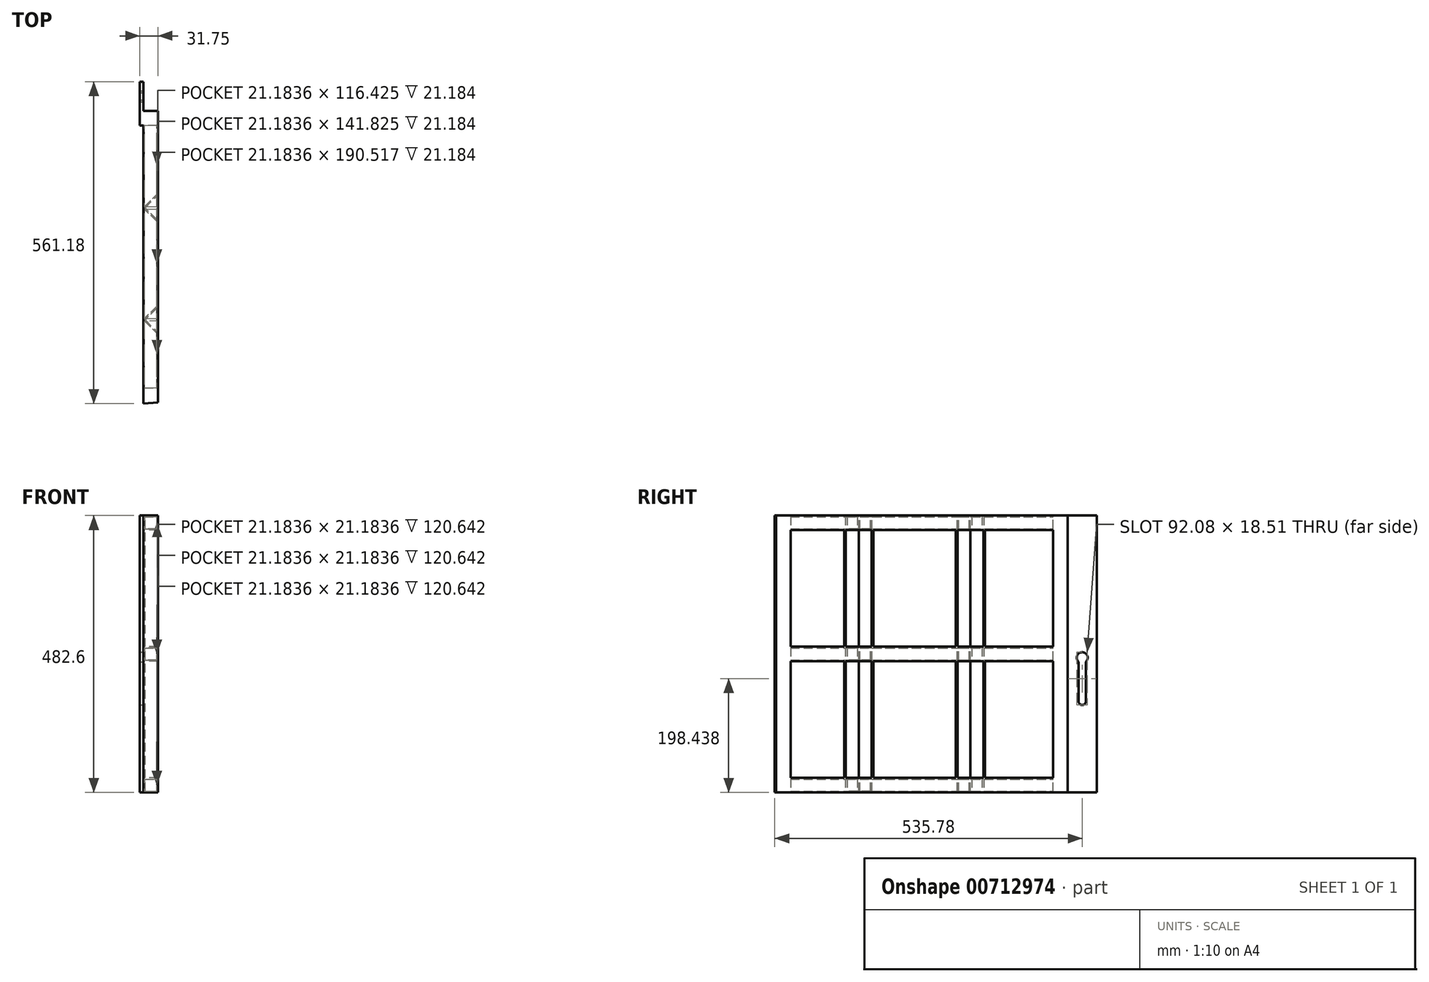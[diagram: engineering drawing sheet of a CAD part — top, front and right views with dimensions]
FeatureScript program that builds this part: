
annotation { "Feature Type Name" : "Feature", "Feature Type Description" : "" }
export const myFeature = defineFeature(function(context is Context, id is Id, definition is map)
    precondition{}
    {
        {
            var Q0;
            Q0=qCreatedBy(makeId("Front.planeOp"),FACE);
            var sketch = newSketch(context, id + "F0", { "sketchPlane" : qUnion([Q0])});
            skLineSegment(sketch, "E0.bottom", {"start": v(-12.7, 12.7) * mm, "end": v(12.7, 12.7) * mm});
            skLineSegment(sketch, "E0.top", {"start": v(-12.7, -12.7) * mm, "end": v(12.7, -12.7) * mm});
            skLineSegment(sketch, "E0.left", {"start": v(-12.7, 12.7) * mm, "end": v(-12.7, -12.7) * mm});
            skLineSegment(sketch, "E0.right", {"start": v(12.7, 12.7) * mm, "end": v(12.7, -12.7) * mm});
            skPoint(sketch, "E0.middle", {"position": v(0, 0) * mm});
            skLineSegment(sketch, "E1.0", {"start": v(-10.6, 10.6) * mm, "end": v(10.6, 10.6) * mm});
            skLineSegment(sketch, "E1.1", {"start": v(-10.6, 10.6) * mm, "end": v(-10.6, -10.6) * mm});
            skLineSegment(sketch, "E1.2", {"start": v(-10.6, -10.6) * mm, "end": v(10.6, -10.6) * mm});
            skLineSegment(sketch, "E1.3", {"start": v(10.6, 10.6) * mm, "end": v(10.6, -10.6) * mm});
            skLineSegment(sketch, "E2.1.0.0", {"start": v(12.7, 241.3) * mm, "end": v(12.7, 215.9) * mm});
            skLineSegment(sketch, "E2.1.0.1", {"start": v(-12.7, 241.3) * mm, "end": v(-12.7, 215.9) * mm});
            skLineSegment(sketch, "E2.1.0.2", {"start": v(-12.7, 215.9) * mm, "end": v(12.7, 215.9) * mm});
            skLineSegment(sketch, "E2.1.0.3", {"start": v(-12.7, 241.3) * mm, "end": v(12.7, 241.3) * mm});
            skLineSegment(sketch, "E2.1.0.4", {"start": v(-10.6, 218) * mm, "end": v(10.6, 218) * mm});
            skPoint(sketch, "E2.1.0.5", {"position": v(0, 228.6) * mm});
            skLineSegment(sketch, "E2.1.0.6", {"start": v(10.6, 239.2) * mm, "end": v(10.6, 218) * mm});
            skLineSegment(sketch, "E2.1.0.7", {"start": v(-10.6, 239.2) * mm, "end": v(10.6, 239.2) * mm});
            skLineSegment(sketch, "E2.1.0.8", {"start": v(-10.6, 239.2) * mm, "end": v(-10.6, 218) * mm});
            skLineSegment(sketch, "E2.2.0.0", {"start": v(12.7, 469.9) * mm, "end": v(12.7, 444.5) * mm});
            skLineSegment(sketch, "E2.2.0.1", {"start": v(-12.7, 469.9) * mm, "end": v(-12.7, 444.5) * mm});
            skLineSegment(sketch, "E2.2.0.2", {"start": v(-12.7, 444.5) * mm, "end": v(12.7, 444.5) * mm});
            skLineSegment(sketch, "E2.2.0.3", {"start": v(-12.7, 469.9) * mm, "end": v(12.7, 469.9) * mm});
            skLineSegment(sketch, "E2.2.0.4", {"start": v(-10.6, 446.6) * mm, "end": v(10.6, 446.6) * mm});
            skPoint(sketch, "E2.2.0.5", {"position": v(0, 457.2) * mm});
            skLineSegment(sketch, "E2.2.0.6", {"start": v(10.6, 467.8) * mm, "end": v(10.6, 446.6) * mm});
            skLineSegment(sketch, "E2.2.0.7", {"start": v(-10.6, 467.8) * mm, "end": v(10.6, 467.8) * mm});
            skLineSegment(sketch, "E2.2.0.8", {"start": v(-10.6, 467.8) * mm, "end": v(-10.6, 446.6) * mm});
            skLineSegment(sketch, "E2.direction1", {"start": v(0, 0) * mm, "end": v(0, 228.6) * mm, "construction": true});
            skSolve(sketch);
        }
        {
            var Q0;
            Q0=makeQuery(id+"F0.imprint","IMPRINT",FACE,{"disambiguationData":[TD([[makeQuery(id+"F0.imprint","IMPRINT",EDGE,{"derivedFrom":sQuery(id+"F0.wireOp",EDGE,"E2.2.0.0")}),-1.0]])]});
            var Q1;
            Q1=makeQuery(id+"F0.imprint","IMPRINT",FACE,{"disambiguationData":[TD([[makeQuery(id+"F0.imprint","IMPRINT",EDGE,{"derivedFrom":sQuery(id+"F0.wireOp",EDGE,"E2.1.0.0")}),-1.0]])]});
            var Q2;
            Q2=makeQuery(id+"F0.imprint","IMPRINT",FACE,{"disambiguationData":[TD([[makeQuery(id+"F0.imprint","IMPRINT",EDGE,{"derivedFrom":sQuery(id+"F0.wireOp",EDGE,"E0.bottom")}),-1.0]])]});
            extrude(context, id + "F1", {"entities" : qUnion([Q0, Q1, Q2]), "depth" : 508 * mm, "offsetDistance" : 25.4 * mm});
        }
        {
            var Q0;
            Q0=makeQuery(id+"F1.opExtrude","SWEPT_FACE",FACE,{"disambiguationData":[OSD([sQuery(id+"F0.wireOp",EDGE,"E2.2.0.3")])]});
            var sketch = newSketch(context, id + "F2", { "sketchPlane" : qUnion([Q0])});
            skLineSegment(sketch, "E3.bottom", {"start": v(12.7, 0) * mm, "end": v(-12.7, 0) * mm});
            skLineSegment(sketch, "E3.top", {"start": v(12.7, -25.4) * mm, "end": v(-12.7, -25.4) * mm});
            skLineSegment(sketch, "E3.left", {"start": v(12.7, 0) * mm, "end": v(12.7, -25.4) * mm});
            skLineSegment(sketch, "E3.right", {"start": v(-12.7, 0) * mm, "end": v(-12.7, -25.4) * mm});
            skLineSegment(sketch, "E4.bottom", {"start": v(-12.7, -508) * mm, "end": v(12.7, -508) * mm});
            skLineSegment(sketch, "E4.top", {"start": v(-12.7, -482.6) * mm, "end": v(12.7, -482.6) * mm});
            skLineSegment(sketch, "E4.left", {"start": v(-12.7, -508) * mm, "end": v(-12.7, -482.6) * mm});
            skLineSegment(sketch, "E4.right", {"start": v(12.7, -508) * mm, "end": v(12.7, -482.6) * mm});
            skSolve(sketch);
        }
        {
            var Q0;
            Q0=makeQuery(id+"F2.imprint","IMPRINT",FACE,{"disambiguationData":[TD([[makeQuery(id+"F2.imprint","IMPRINT",EDGE,{"derivedFrom":sQuery(id+"F2.wireOp",EDGE,"E3.bottom")}),-1.0]])]});
            var Q1;
            Q1=makeQuery(id+"F2.imprint","IMPRINT",FACE,{"disambiguationData":[TD([[makeQuery(id+"F2.imprint","IMPRINT",EDGE,{"derivedFrom":sQuery(id+"F2.wireOp",EDGE,"E4.bottom")}),1.0]])]});
            extrude(context, id + "F3", {"entities" : qUnion([Q0, Q1]), "operationType" : NewBodyOperationType.ADD, "oppositeDirection" : true, "depth" : 482.6 * mm, "offsetDistance" : 25.4 * mm});
        }
        {
            var Q0;
            Q0=makeQuery(id+"F3.boolean.opBoolean","MERGE",FACE,{"derivedFrom":[makeQuery(id+"F1.opExtrude","SWEPT_FACE",FACE,{"disambiguationData":[OSD([sQuery(id+"F0.wireOp",EDGE,"E0.left")])]}),makeQuery(id+"F1.opExtrude","SWEPT_FACE",FACE,{"disambiguationData":[OSD([sQuery(id+"F0.wireOp",EDGE,"E2.1.0.1")])]}),makeQuery(id+"F1.opExtrude","SWEPT_FACE",FACE,{"disambiguationData":[OSD([sQuery(id+"F0.wireOp",EDGE,"E2.2.0.1")])]}),makeQuery(id+"F3.opExtrude","SWEPT_FACE",FACE,{"disambiguationData":[OSD([sQuery(id+"F2.wireOp",EDGE,"E3.right")])]}),makeQuery(id+"F3.opExtrude","SWEPT_FACE",FACE,{"disambiguationData":[OSD([sQuery(id+"F2.wireOp",EDGE,"E4.left")])]})]});
            var sketch = newSketch(context, id + "F4", { "sketchPlane" : qUnion([Q0])});
            skLineSegment(sketch, "E5.bottom", {"start": v(-50.8, -12.7) * mm, "end": v(25.4, -12.7) * mm});
            skLineSegment(sketch, "E5.top", {"start": v(-50.8, 469.9) * mm, "end": v(25.4, 469.9) * mm});
            skLineSegment(sketch, "E5.left", {"start": v(-50.8, -12.7) * mm, "end": v(-50.8, 469.9) * mm});
            skLineSegment(sketch, "E5.right", {"start": v(25.4, -12.7) * mm, "end": v(25.4, 469.9) * mm});
            skArc(sketch, "E6", {"start": v(-19.05, 215.15) * mm, "mid": v(-25.4, 231.78) * mm, "end": v(-31.75, 215.15) * mm});
            skArc(sketch, "E7", {"start": v(-31.75, 146.05) * mm, "mid": v(-25.4, 139.7) * mm, "end": v(-19.05, 146.05) * mm});
            skLineSegment(sketch, "E8", {"start": v(-19.05, 146.05) * mm, "end": v(-19.05, 215.15) * mm});
            skLineSegment(sketch, "E9", {"start": v(-31.75, 146.05) * mm, "end": v(-31.75, 215.15) * mm});
            skSolve(sketch);
        }
        {
            var Q0;
            Q0=qSketchRegion(id+"F4",true);
            extrude(context, id + "F5", {"entities" : qUnion([Q0]), "operationType" : NewBodyOperationType.ADD, "depth" : 6.35 * mm, "offsetDistance" : 25.4 * mm});
        }
        {
            var Q0;
            Q0=makeQuery(id+"F5.boolean.opBoolean","MERGE",FACE,{"derivedFrom":[makeQuery(id+"F1.opExtrude","SWEPT_FACE",FACE,{"disambiguationData":[OSD([sQuery(id+"F0.wireOp",EDGE,"E2.2.0.3")])]}),makeQuery(id+"F5.opExtrude","SWEPT_FACE",FACE,{"disambiguationData":[OSD([sQuery(id+"F4.wireOp",EDGE,"E5.top")])]})]});
            var sketch = newSketch(context, id + "F6", { "sketchPlane" : qUnion([Q0])});
            skLineSegment(sketch, "E10", {"start": v(12.7, -194.73) * mm, "end": v(-12.7, -169.33) * mm});
            skLineSegment(sketch, "E11", {"start": v(-12.7, -169.33) * mm, "end": v(12.7, -143.93) * mm});
            skLineSegment(sketch, "E12.0", {"start": v(-9.72, -169.33) * mm, "end": v(12.7, -146.91) * mm});
            skLineSegment(sketch, "E12.1", {"start": v(12.7, -191.75) * mm, "end": v(-9.72, -169.33) * mm});
            skLineSegment(sketch, "E13", {"start": v(12.7, -194.73) * mm, "end": v(12.7, -191.75) * mm});
            skLineSegment(sketch, "E14", {"start": v(12.7, -143.93) * mm, "end": v(12.7, -146.91) * mm});
            skLineSegment(sketch, "E15", {"start": v(-12.7, -266.7) * mm, "end": v(12.7, -266.7) * mm, "construction": true});
            skLineSegment(sketch, "E16.MirrorCS", {"start": v(12.7, -389.47) * mm, "end": v(12.7, -386.49) * mm});
            skLineSegment(sketch, "E17.MirrorCS", {"start": v(12.7, -338.67) * mm, "end": v(12.7, -341.65) * mm});
            skLineSegment(sketch, "E18.MirrorCS", {"start": v(12.7, -341.65) * mm, "end": v(-9.72, -364.07) * mm});
            skLineSegment(sketch, "E19.MirrorCS", {"start": v(-9.72, -364.07) * mm, "end": v(12.7, -386.49) * mm});
            skLineSegment(sketch, "E20.MirrorCS", {"start": v(-12.7, -364.07) * mm, "end": v(12.7, -389.47) * mm});
            skLineSegment(sketch, "E21.MirrorCS", {"start": v(12.7, -338.67) * mm, "end": v(-12.7, -364.07) * mm});
            skSolve(sketch);
        }
        {
            var Q0;
            Q0=qSketchRegion(id+"F6",true);
            extrude(context, id + "F7", {"entities" : qUnion([Q0]), "operationType" : NewBodyOperationType.ADD, "oppositeDirection" : true, "depth" : 482.6 * mm, "offsetDistance" : 25.4 * mm});
        }
        {
            var Q0;
            Q0=makeQuery(id+"F5.boolean.opBoolean","MERGE",FACE,{"derivedFrom":[makeQuery(id+"F1.opExtrude","SWEPT_FACE",FACE,{"disambiguationData":[OSD([sQuery(id+"F0.wireOp",EDGE,"E2.2.0.3")])]}),makeQuery(id+"F5.opExtrude","SWEPT_FACE",FACE,{"disambiguationData":[OSD([sQuery(id+"F4.wireOp",EDGE,"E5.top")])]})]});
            var sketch = newSketch(context, id + "F8", { "sketchPlane" : qUnion([Q0])});
            skLineSegment(sketch, "E22", {"start": v(12.7, -508) * mm, "end": v(-12.7, -510.38) * mm});
            skLineSegment(sketch, "E23", {"start": v(-12.7, -510.38) * mm, "end": v(-12.7, -508) * mm});
            skLineSegment(sketch, "E24", {"start": v(-12.7, -508) * mm, "end": v(12.7, -508) * mm});
            skSolve(sketch);
        }
        {
            var Q0;
            Q0=makeQuery(id+"F8.imprint","IMPRINT",FACE,{"disambiguationData":[TD([[makeQuery(id+"F8.imprint","IMPRINT",EDGE,{"derivedFrom":sQuery(id+"F8.wireOp",EDGE,"E22")}),-1.0]])]});
            extrude(context, id + "F9", {"entities" : qUnion([Q0]), "operationType" : NewBodyOperationType.ADD, "oppositeDirection" : true, "depth" : 482.6 * mm, "offsetDistance" : 25.4 * mm});
        }
    });
